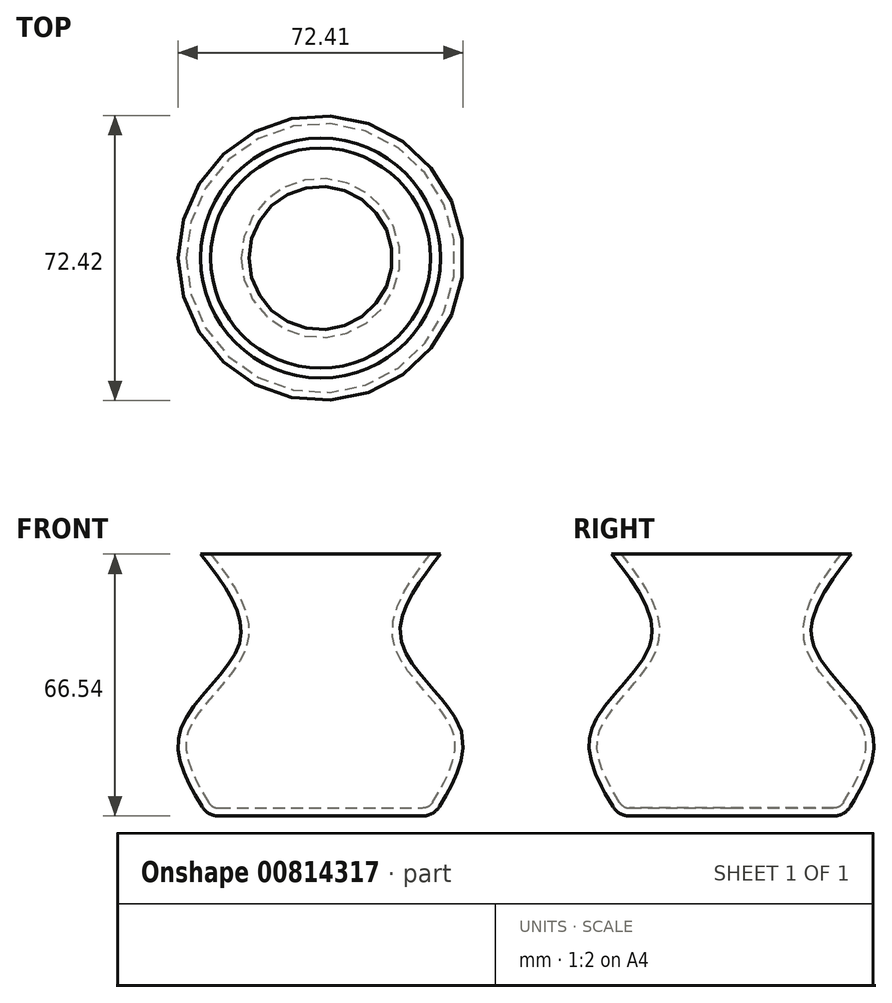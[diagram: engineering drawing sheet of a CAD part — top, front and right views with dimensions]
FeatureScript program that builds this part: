
annotation { "Feature Type Name" : "Feature", "Feature Type Description" : "" }
export const myFeature = defineFeature(function(context is Context, id is Id, definition is map)
    precondition{}
    {
        {
            var Q0;
            Q0=qCreatedBy(makeId("Front.planeOp"),FACE);
            var sketch = newSketch(context, id + "F0", { "sketchPlane" : qUnion([Q0])});
            skFitSpline(sketch, "E0", {"points": [v(-30.47, 63.86) * mm, v(-20.57, 41.47) * mm, v(-35.6, 19.2) * mm, v(-28.68, -2.68) * mm], "startDerivative": vector(53.4, -68.69) * mm, "endDerivative": vector(43.07, -69.41) * mm});
            skLineSegment(sketch, "E1", {"start": v(0, 0) * mm, "end": v(0, 72.45) * mm, "construction": true});
            skLineSegment(sketch, "E2", {"start": v(-28.68, -2.68) * mm, "end": v(0, -2.68) * mm});
            skLineSegment(sketch, "E3", {"start": v(0, -2.68) * mm, "end": v(0, 63.86) * mm});
            skLineSegment(sketch, "E4", {"start": v(0, 63.86) * mm, "end": v(-30.47, 63.86) * mm});
            skSolve(sketch);
        }
        {
            var Q0;
            Q0=makeQuery(id+"F0.imprint","IMPRINT",FACE,{"disambiguationData":[TD([[makeQuery(id+"F0.imprint","IMPRINT",EDGE,{"derivedFrom":sQuery(id+"F0.wireOp",EDGE,"E0")}),1.0]])]});
            var Q1;
            Q1=sQuery(id+"F0.wireOp",EDGE,"E3");
            revolve(context, id + "F1", {"surfaceOperationType" : NewSurfaceOperationType.NEW, "entities" : qUnion([Q0]), "axis" : qUnion([Q1]), "revolveType" : RevolveType.FULL});
        }
        {
            var Q0;
            Q0=makeQuery(id+"F1.opRevolve","SWEPT_EDGE",EDGE,{"disambiguationData":[OSD([sQuery(id+"F0.wireOp",EDGE,"E0"),sQuery(id+"F0.wireOp",EDGE,"E2")])]});
            fillet(context, id + "F2", {"entities" : qUnion([Q0]), "radius" : 5 * mm, "tangentPropagation" : true, "allowEdgeOverflow" : false});
        }
        {
            var Q0;
            Q0=makeQuery(id+"F1.opRevolve","SWEPT_FACE",FACE,{"disambiguationData":[OSD([sQuery(id+"F0.wireOp",EDGE,"E4")])]});
            shell(context, id + "F3", {"entities" : qUnion([Q0]), "thickness" : 2 * mm});
        }
    });
